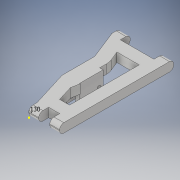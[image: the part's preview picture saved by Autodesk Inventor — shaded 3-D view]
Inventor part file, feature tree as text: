
AUTODESK INVENTOR PART (.ipt)
format: ipt  version: 2018 (Build 220112000, 112)  size: 230,400 bytes
history: native  units: in
note: dims shown in document units (in); Inventor stores cm internally (conversion verified against a paired STEP export)
features: sketch x6, extrude x4, fillet x1, projected_geometry x1
ambient origin geometry x8: Origin, YZ Plane, XZ Plane, XY Plane, X Axis, Y Axis, Z Axis, Center Point
bodies: Solid1 (feature_tree)
feature tree (12):
  extrude  "Extrusion1"  Depth=1.625in
  fillet  "Fillet2"  Radius=0.9375in
  extrude  "Extrusion2"  Depth=1.277in
  sketch  "Sketch3"  dims[d5=1.0in d6=0.5in]
  extrude  "Extrusion3"  Depth=0.5in
  extrude  "Extrusion4"  Depth=0.25in
  sketch  "Sketch6"  dims[d12=0.3in d13=0.3in d14=0.3in d15=0.3in d16=0.3in d17=0.3in d18=0.125in d19=0.375in d20=0.275in d21=0.0in d22=0.125in d24=0.2275in d25=0.125in d26=0.125in d28=0.5497in d29=0.125in d30=0.125in d31=0.7in d32=0.0in d33=0.1in d34=0.58in d35=0.1in d36=0.26in d37=0.1in d38=0.26in d39=0.4in d40=0.14in d41=1.0in d42=0.0in d43=0.75in d44=0.75in d45=0.75in d46=0.75in d47=0.13in]
  sketch  "Sketch1"  dims[d0=3.475in d1=1.625in d2=0.9375in]
  sketch  "Sketch2"  dims[d3=1.625in d4=1.277in]
  projected_geometry  "Projected Loop1"
  sketch  "Sketch4"  dims[d8=0.0in d10=0.25in]
  sketch  "Sketch5"  dims[d11=0.25in]
